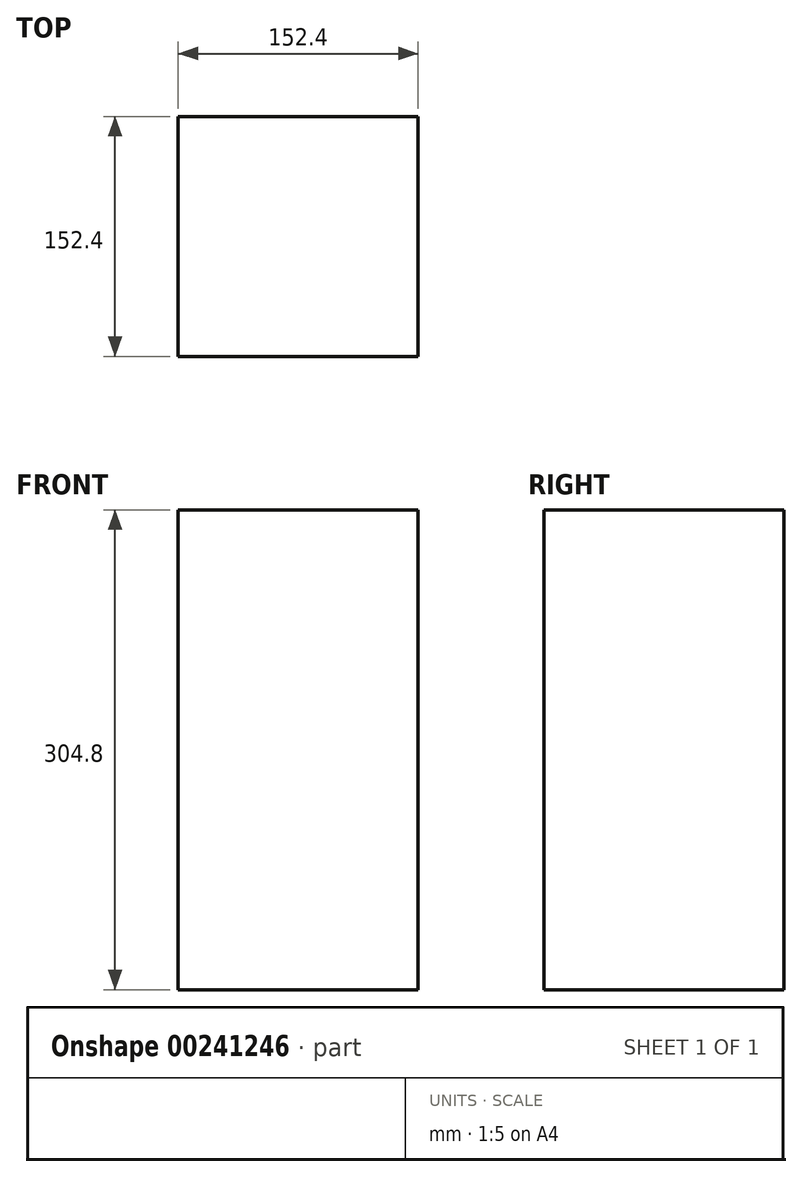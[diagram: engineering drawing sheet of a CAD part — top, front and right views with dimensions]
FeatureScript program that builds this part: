
annotation { "Feature Type Name" : "Feature", "Feature Type Description" : "" }
export const myFeature = defineFeature(function(context is Context, id is Id, definition is map)
    precondition{}
    {
        {
            var Q0;
            Q0=qCreatedBy(makeId("Top.planeOp"),FACE);
            var sketch = newSketch(context, id + "F0", { "sketchPlane" : qUnion([Q0])});
            skLineSegment(sketch, "E0.bottom", {"start": v(76.2, -77.1) * mm, "end": v(-76.2, -77.1) * mm});
            skLineSegment(sketch, "E0.top", {"start": v(76.2, 75.3) * mm, "end": v(-76.2, 75.3) * mm});
            skLineSegment(sketch, "E0.left", {"start": v(76.2, -77.1) * mm, "end": v(76.2, 75.3) * mm});
            skLineSegment(sketch, "E0.right", {"start": v(-76.2, -77.1) * mm, "end": v(-76.2, 75.3) * mm});
            skSolve(sketch);
        }
        {
            var Q0;
            Q0=makeQuery(id+"F0.imprint","IMPRINT",FACE,{"disambiguationData":[TD([[makeQuery(id+"F0.imprint","IMPRINT",EDGE,{"derivedFrom":sQuery(id+"F0.wireOp",EDGE,"E0.bottom")}),-1.0]])]});
            extrude(context, id + "F1", {"entities" : qUnion([Q0]), "oppositeDirection" : true, "depth" : 304.8 * mm});
        }
    });
